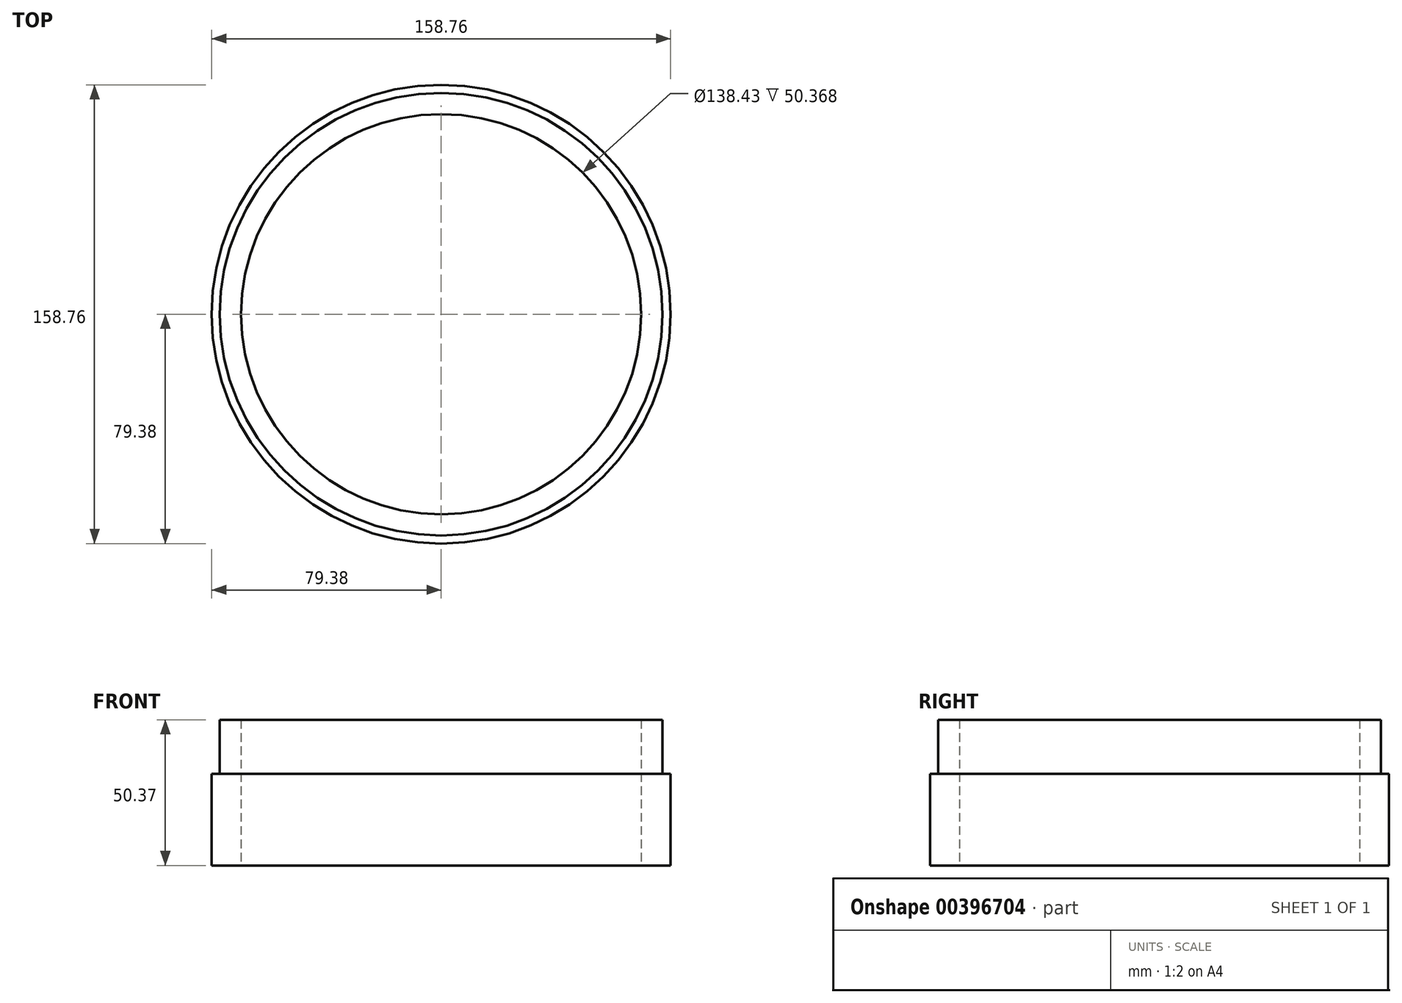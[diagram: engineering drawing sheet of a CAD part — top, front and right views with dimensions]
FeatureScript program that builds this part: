
annotation { "Feature Type Name" : "Feature", "Feature Type Description" : "" }
export const myFeature = defineFeature(function(context is Context, id is Id, definition is map)
    precondition{}
    {
        {
            var Q0;
            Q0=qCreatedBy(makeId("Right.planeOp"),FACE);
            var sketch = newSketch(context, id + "F0", { "sketchPlane" : qUnion([Q0])});
            skLineSegment(sketch, "E0", {"start": v(69.22, 0) * mm, "end": v(69.22, 50.37) * mm});
            skLineSegment(sketch, "E1", {"start": v(69.22, 50.37) * mm, "end": v(76.58, 50.37) * mm});
            skLineSegment(sketch, "E2", {"start": v(76.58, 50.37) * mm, "end": v(76.58, 31.75) * mm});
            skLineSegment(sketch, "E3", {"start": v(76.58, 31.75) * mm, "end": v(79.38, 31.75) * mm});
            skLineSegment(sketch, "E4", {"start": v(79.38, 31.75) * mm, "end": v(79.38, 0) * mm});
            skLineSegment(sketch, "E5", {"start": v(79.38, 0) * mm, "end": v(69.22, 0) * mm});
            skSolve(sketch);
        }
        {
            var Q0;
            Q0=qCreatedBy(makeId("Right.planeOp"),FACE);
            var sketch = newSketch(context, id + "F1", { "sketchPlane" : qUnion([Q0])});
            skLineSegment(sketch, "E6", {"start": v(0, 0) * mm, "end": v(0, 48.5) * mm});
            skSolve(sketch);
        }
        {
            var Q0;
            Q0 = qSketchRegion(id + "F0", true);
            var Q1;
            Q1=sQuery(id+"F1.wireOp",EDGE,"E6");
            revolve(context, id + "F2", {"entities" : qUnion([Q0]), "axis" : qUnion([Q1]), "revolveType" : RevolveType.FULL});
        }
    });
